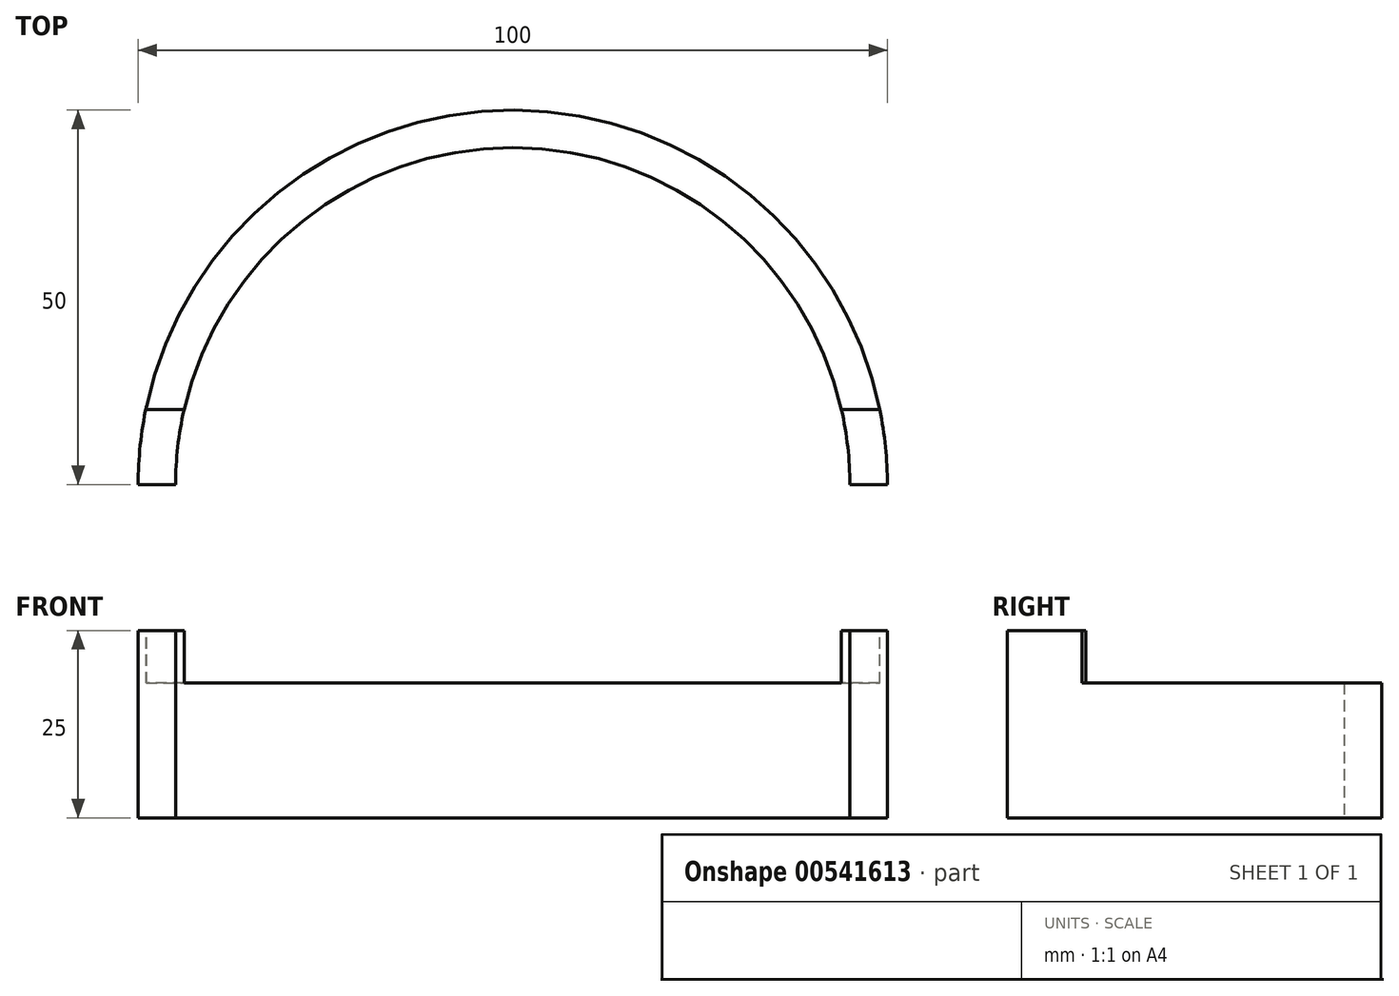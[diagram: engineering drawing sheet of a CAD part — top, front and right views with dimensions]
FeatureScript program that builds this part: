
annotation { "Feature Type Name" : "Feature", "Feature Type Description" : "" }
export const myFeature = defineFeature(function(context is Context, id is Id, definition is map)
    precondition{}
    {
        {
            var Q0;
            Q0=qCreatedBy(makeId("Top.planeOp"),FACE);
            var sketch = newSketch(context, id + "F0", { "sketchPlane" : qUnion([Q0])});
            skArc(sketch, "E0", {"start": v(100, 0) * mm, "mid": v(50, 50) * mm, "end": v(0, 0) * mm});
            skArc(sketch, "E1.0", {"start": v(95, 0) * mm, "mid": v(50, 45) * mm, "end": v(5, 0) * mm});
            skLineSegment(sketch, "E2", {"start": v(0, 0) * mm, "end": v(5, 0) * mm});
            skLineSegment(sketch, "E3", {"start": v(95, 0) * mm, "end": v(100, 0) * mm});
            skSolve(sketch);
        }
        {
            var Q0;
            Q0 = qSketchRegion(id + "F0", true);
            extrude(context, id + "F1", {"entities" : qUnion([Q0]), "depth" : 25 * mm, "offsetDistance" : 25 * mm});
        }
        {
            var Q0;
            Q0=makeQuery(id+"F1.opExtrude","CAP_FACE",FACE,{"disambiguationData":[OSD([sQuery(id+"F0.wireOp",EDGE,"E0"),sQuery(id+"F0.wireOp",EDGE,"E1.0"),sQuery(id+"F0.wireOp",EDGE,"E2"),sQuery(id+"F0.wireOp",EDGE,"E3")])],"isStart":false});
            var sketch = newSketch(context, id + "F2", { "sketchPlane" : qUnion([Q0])});
            skLineSegment(sketch, "E4", {"start": v(1.05, 10) * mm, "end": v(6.18, 10) * mm});
            skLineSegment(sketch, "E5", {"start": v(93.87, 10) * mm, "end": v(98.99, 10) * mm});
            skArc(sketch, "E6", {"start": v(98.99, 10) * mm, "mid": v(50.02, 53.74) * mm, "end": v(1.05, 10) * mm});
            skArc(sketch, "E7", {"start": v(93.87, 10) * mm, "mid": v(50.03, 31.97) * mm, "end": v(6.18, 10) * mm});
            skSolve(sketch);
        }
        {
            var Q0;
            Q0 = qSketchRegion(id + "F2", true);
            extrude(context, id + "F3", {"entities" : qUnion([Q0]), "operationType" : NewBodyOperationType.REMOVE, "oppositeDirection" : true, "depth" : 7 * mm, "offsetDistance" : 25 * mm});
        }
    });
